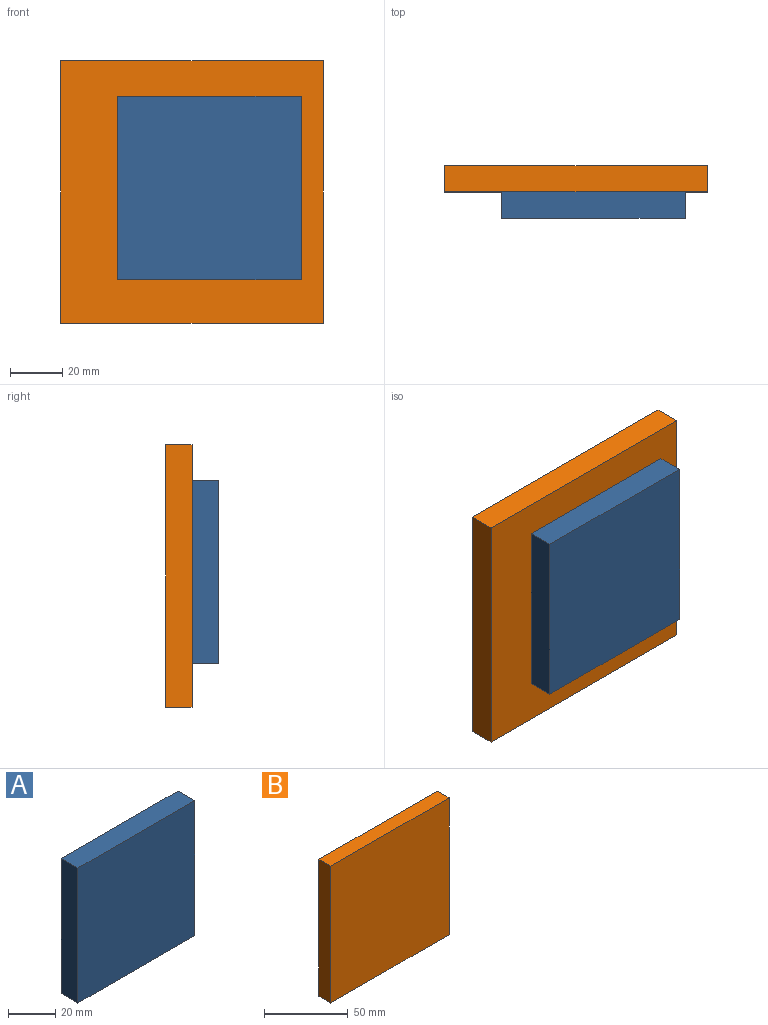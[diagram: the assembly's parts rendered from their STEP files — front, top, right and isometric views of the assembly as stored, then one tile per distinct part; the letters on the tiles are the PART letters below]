
ASSEMBLY  parts=2 mates=1
PART A: 6 faces, bbox 70x10x70 mm
  f0: plane 70x10mm, normal (0,0,1), area 700mm2, adj f1,f3,f4,f5
  f1: plane 70x10mm, normal (-1,0,0), area 700mm2, adj f0,f2,f4,f5
  f2: plane 70x10mm, normal (0,0,-1), area 700mm2, adj f1,f3,f4,f5
  f3: plane 70x10mm, normal (1,0,0), area 700mm2, adj f0,f2,f4,f5
  f4: plane 70x70mm, normal (0,-1,0), area 4900mm2, adj f0,f1,f2,f3
  f5: plane 70x70mm, normal (0,1,0), area 4900mm2, adj f0,f1,f2,f3
PART B: 6 faces, bbox 100x10x100 mm
  f0: plane 100x10mm, normal (0,0,1), area 1000mm2, adj f1,f3,f4,f5
  f1: plane 100x10mm, normal (-1,0,0), area 1000mm2, adj f0,f2,f4,f5
  f2: plane 100x10mm, normal (0,0,-1), area 1000mm2, adj f1,f3,f4,f5
  f3: plane 100x10mm, normal (1,0,0), area 1000mm2, adj f0,f2,f4,f5
  f4: plane 100x100mm, normal (0,-1,0), area 10000mm2, adj f0,f1,f2,f3
  f5: plane 100x100mm, normal (0,1,0), area 10000mm2, adj f0,f1,f2,f3
PLACE A t=(7.17,-4.73,1.4)mm
PLACE B t=(0.72,5.27,1)mm fixed
MATE planar B.f4 <-> A.f5  axis (0,-1,0) through (0.56,-4.73,-0.08)mm
